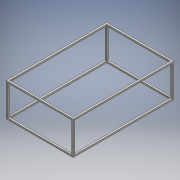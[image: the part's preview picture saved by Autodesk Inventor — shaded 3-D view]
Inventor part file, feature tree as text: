
AUTODESK INVENTOR PART (.ipt)
format: ipt  version: 2016 (Build 200138000, 138)  size: 139,776 bytes
history: native  units: mm
features: extrude x4, sketch x3
ambient origin geometry x8: Origin, YZ Plane, XZ Plane, XY Plane, X Axis, Y Axis, Z Axis, Center Point
bodies: Solid1 (feature_tree)
feature tree (7):
  extrude  "Extrusion1"  Depth=200.0mm
  extrude  "Extrusion2"  Depth=5.0mm
  extrude  "Extrusion3"  Depth=5.0mm
  extrude  "Extrusion4"  Depth=5.0mm
  sketch  "Sketch3"  dims[d0=100.0mm d1=200.0mm]
  sketch  "Sketch4"  dims[d6=300.0mm d7=0.0mm d8=5.0mm]
  sketch  "Sketch6"  dims[d9=5.0mm d10=5.0mm d11=5.0mm d12=10.0mm d13=0.0mm d14=5.0mm d15=5.0mm d16=5.0mm d17=5.0mm d18=10.0mm d19=0.0mm d20=5.0mm d21=5.0mm d22=5.0mm d23=5.0mm d24=10.0mm d25=0.0mm]
